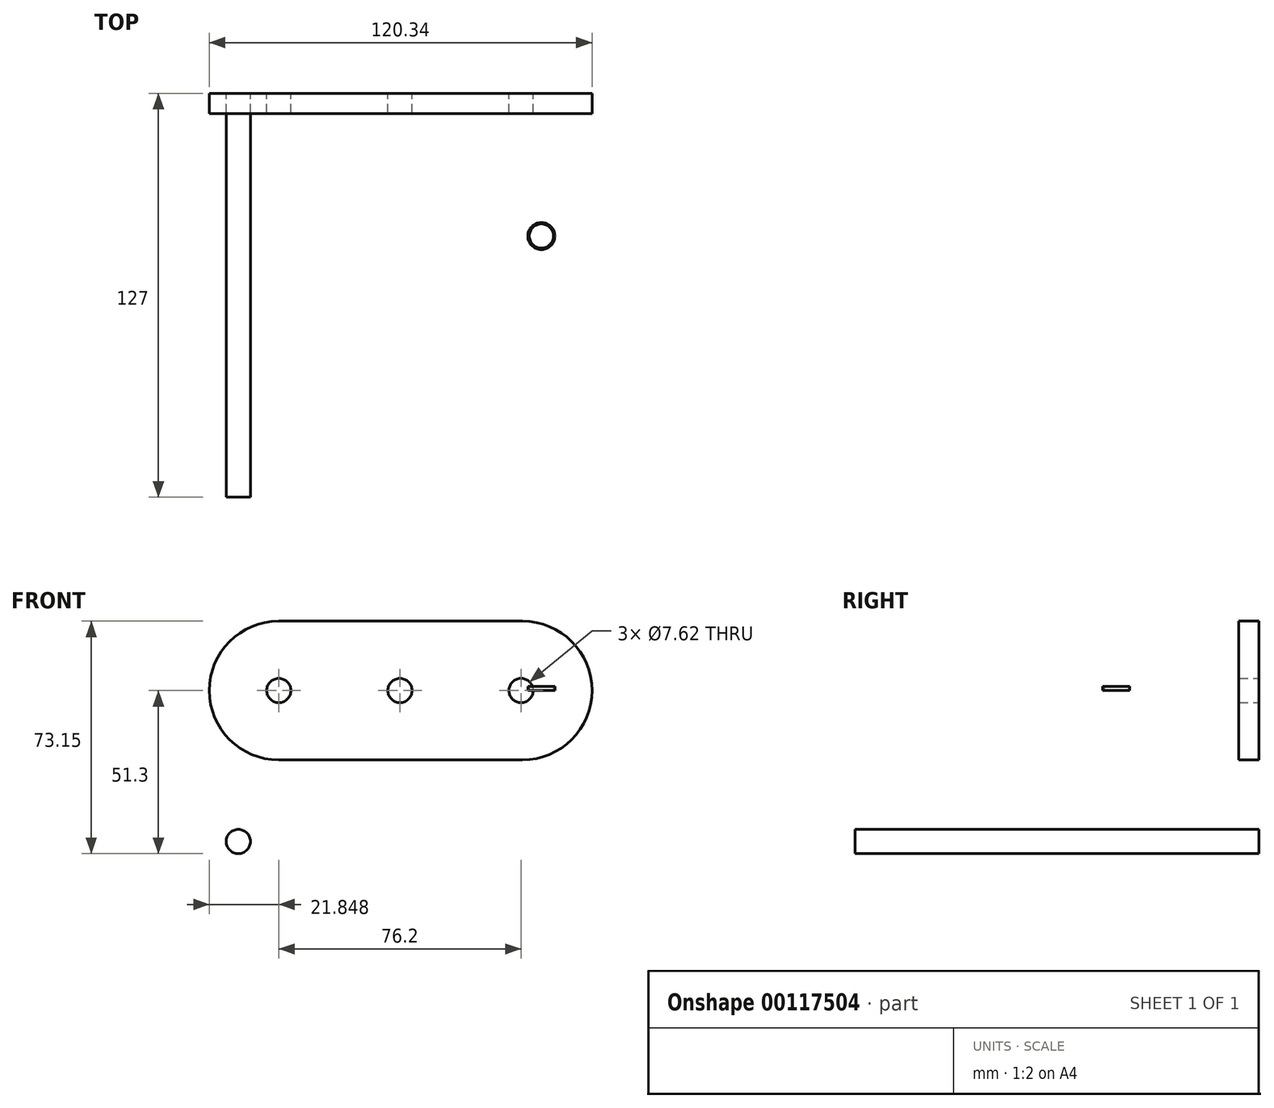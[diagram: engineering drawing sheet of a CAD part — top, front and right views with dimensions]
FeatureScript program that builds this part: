
annotation { "Feature Type Name" : "Feature", "Feature Type Description" : "" }
export const myFeature = defineFeature(function(context is Context, id is Id, definition is map)
    precondition{}
    {
        {
            var Q0;
            Q0=qCreatedBy(makeId("Front.planeOp"),FACE);
            var sketch = newSketch(context, id + "F0", { "sketchPlane" : qUnion([Q0])});
            skLineSegment(sketch, "E0.bottom", {"start": v(38.32, -21.85) * mm, "end": v(-38.32, -21.85) * mm});
            skLineSegment(sketch, "E0.top", {"start": v(38.32, 21.85) * mm, "end": v(-38.32, 21.85) * mm});
            skPoint(sketch, "E0.middle", {"position": v(0, 0) * mm});
            skArc(sketch, "E1", {"start": v(-38.32, 21.85) * mm, "mid": v(-60.17, 0) * mm, "end": v(-38.32, -21.85) * mm});
            skPoint(sketch, "E1.centerSnap0", {"position": v(-38.32, 0) * mm});
            skArc(sketch, "E2.MirrorCS", {"start": v(38.32, 21.85) * mm, "mid": v(60.17, 0) * mm, "end": v(38.32, -21.85) * mm});
            skCircle(sketch, "E3", {"center": v(-38.32, 0) * mm, "radius": 3.81 * mm});
            skCircle(sketch, "E4.1.0.0", {"center": v(-0.22, 0) * mm, "radius": 3.81 * mm});
            skCircle(sketch, "E4.2.0.0", {"center": v(37.88, 0) * mm, "radius": 3.81 * mm});
            skLineSegment(sketch, "E4.direction1", {"start": v(-38.32, 0) * mm, "end": v(-0.22, 0) * mm, "construction": true});
            skSolve(sketch);
        }
        {
            var Q0;
            Q0=makeQuery(id+"F0.imprint","IMPRINT",FACE,{"disambiguationData":[TD([[makeQuery(id+"F0.imprint","IMPRINT",EDGE,{"derivedFrom":sQuery(id+"F0.wireOp",EDGE,"E0.bottom")}),-1.0]])]});
            extrude(context, id + "F1", {"entities" : qUnion([Q0]), "depth" : 6.35 * mm});
        }
        {
            var Q0;
            Q0=qCreatedBy(makeId("Front.planeOp"),FACE);
            var sketch = newSketch(context, id + "F2", { "sketchPlane" : qUnion([Q0])});
            skCircle(sketch, "E5", {"center": v(-51.06, -47.5) * mm, "radius": 3.81 * mm});
            skSolve(sketch);
        }
        {
            var Q0;
            Q0=makeQuery(id+"F2.imprint","IMPRINT",FACE,{"disambiguationData":[TD([[makeQuery(id+"F2.imprint","IMPRINT",EDGE,{"derivedFrom":sQuery(id+"F2.wireOp",EDGE,"E5")}),1.0]])]});
            extrude(context, id + "F3", {"entities" : qUnion([Q0]), "depth" : 127 * mm});
        }
        {
            var Q0;
            Q0=makeQuery(id+"F3.opExtrude","SWEPT_BODY",BODY,{"disambiguationData":[OSD([sQuery(id+"F2.wireOp",EDGE,"E5")])]});
            transform(context, id + "F4", {"entities" : qUnion([Q0]), "transformType" : TransformType.TRANSLATION_3D, "dx" : 0 * mm, "dy" : 0 * mm, "dz" : 0 * mm, "makeCopy" : true});
        }
        {
            var Q0;
            Q0=makeQuery(id+"F4.opPattern","COPY",BODY,{"derivedFrom":makeQuery(id+"F3.opExtrude","SWEPT_BODY",BODY,{"disambiguationData":[OSD([sQuery(id+"F2.wireOp",EDGE,"E5")])]}),"instanceName":"1"});
            deleteBodies(context, id + "F5", {"entities" : qUnion([Q0])});
        }
        {
            var Q0;
            Q0=makeQuery(id+"F3.opExtrude","SWEPT_BODY",BODY,{"disambiguationData":[OSD([sQuery(id+"F2.wireOp",EDGE,"E5")])]});
            transform(context, id + "F6", {"entities" : qUnion([Q0]), "transformType" : TransformType.TRANSLATION_3D, "dx" : 0 * mm, "dy" : 0 * mm, "dz" : 0 * mm, "makeCopy" : true});
        }
        {
            var Q0;
            Q0=makeQuery(id+"F6.opPattern","COPY",BODY,{"derivedFrom":makeQuery(id+"F3.opExtrude","SWEPT_BODY",BODY,{"disambiguationData":[OSD([sQuery(id+"F2.wireOp",EDGE,"E5")])]}),"instanceName":"1"});
            deleteBodies(context, id + "F7", {"entities" : qUnion([Q0])});
        }
        {
            var Q0;
            Q0=makeQuery(id+"F3.opExtrude","SWEPT_BODY",BODY,{"disambiguationData":[OSD([sQuery(id+"F2.wireOp",EDGE,"E5")])]});
            transform(context, id + "F8", {"entities" : qUnion([Q0]), "transformType" : TransformType.TRANSLATION_3D, "dx" : 50.16 * mm, "dy" : 0 * mm, "dz" : 0 * mm, "makeCopy" : true});
        }
        {
            var Q0;
            Q0=makeQuery(id+"F8.opPattern","COPY",BODY,{"derivedFrom":makeQuery(id+"F3.opExtrude","SWEPT_BODY",BODY,{"disambiguationData":[OSD([sQuery(id+"F2.wireOp",EDGE,"E5")])]}),"instanceName":"1"});
            transform(context, id + "F9", {"entities" : qUnion([Q0]), "transformType" : TransformType.TRANSLATION_3D, "dx" : 42.6 * mm, "dy" : 0 * mm, "dz" : 0 * mm, "makeCopy" : true});
        }
        {
            var Q0;
            Q0=makeQuery(id+"F8.opPattern","COPY",BODY,{"derivedFrom":makeQuery(id+"F3.opExtrude","SWEPT_BODY",BODY,{"disambiguationData":[OSD([sQuery(id+"F2.wireOp",EDGE,"E5")])]}),"instanceName":"1"});
            deleteBodies(context, id + "F10", {"entities" : qUnion([Q0])});
        }
        {
            var Q0;
            Q0=makeQuery(id+"F9.opPattern","COPY",BODY,{"derivedFrom":makeQuery(id+"F8.opPattern","COPY",BODY,{"derivedFrom":makeQuery(id+"F3.opExtrude","SWEPT_BODY",BODY,{"disambiguationData":[OSD([sQuery(id+"F2.wireOp",EDGE,"E5")])]}),"instanceName":"1"}),"instanceName":"1"});
            deleteBodies(context, id + "F11", {"entities" : qUnion([Q0])});
        }
        {
            var Q0;
            Q0=qCreatedBy(makeId("Top.planeOp"),FACE);
            var sketch = newSketch(context, id + "F12", { "sketchPlane" : qUnion([Q0])});
            skCircle(sketch, "E6", {"center": v(44.26, -44.86) * mm, "radius": 4.25 * mm});
            skCircle(sketch, "E7", {"center": v(44.26, -44.86) * mm, "radius": 3.81 * mm});
            skSolve(sketch);
        }
        {
            var Q0;
            Q0 = qSketchRegion(id + "F12", true);
            extrude(context, id + "F13", {"entities" : qUnion([Q0]), "depth" : 1.27 * mm});
        }
    });
